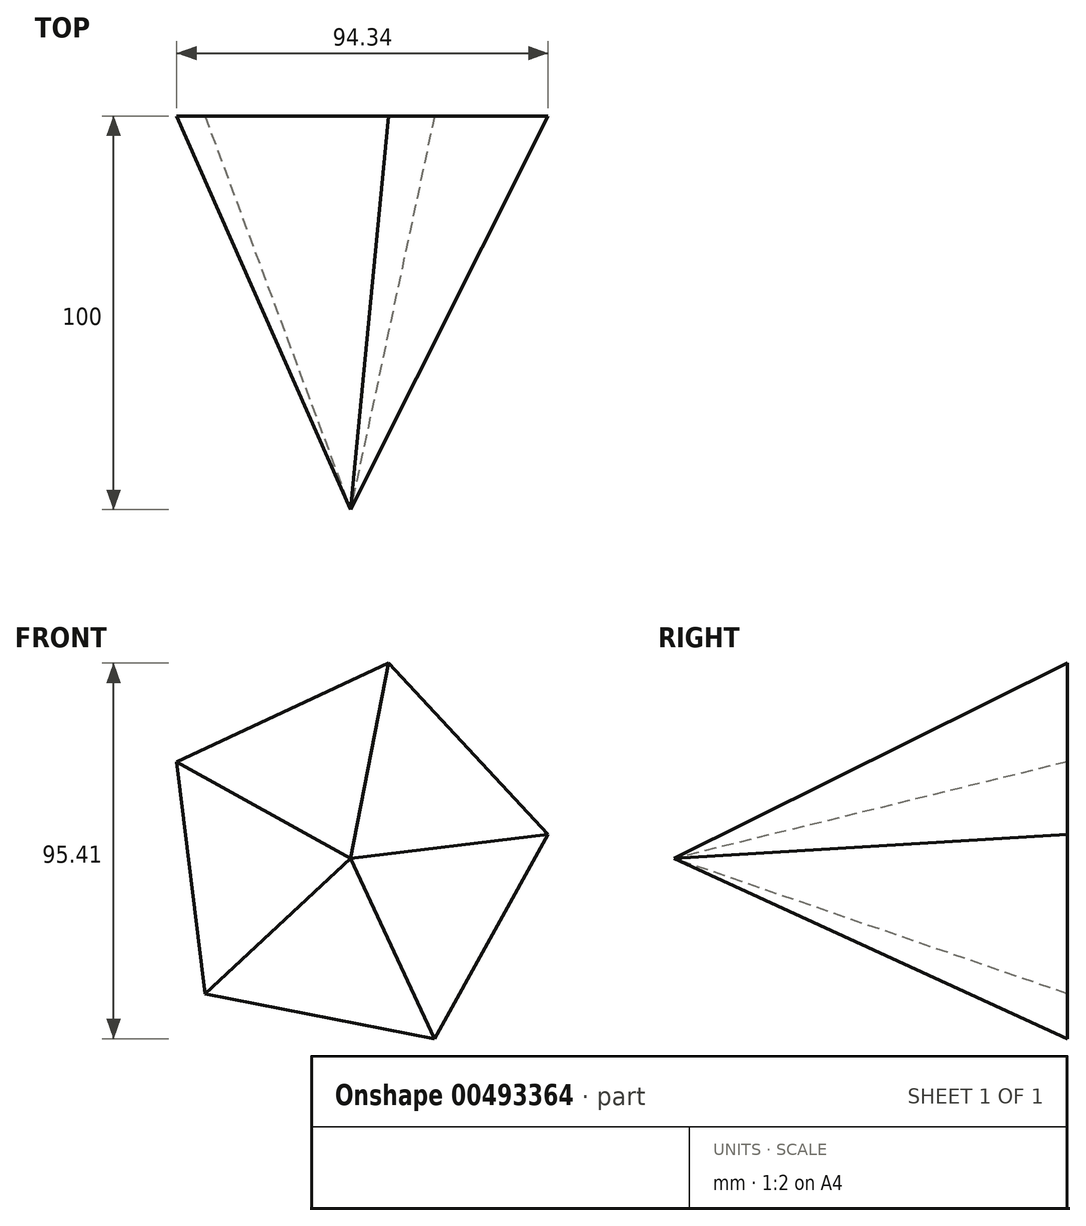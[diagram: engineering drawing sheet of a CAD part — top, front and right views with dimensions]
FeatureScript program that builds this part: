
annotation { "Feature Type Name" : "Feature", "Feature Type Description" : "" }
export const myFeature = defineFeature(function(context is Context, id is Id, definition is map)
    precondition{}
    {
        {
            var Q0;
            Q0=qCreatedBy(makeId("Front.planeOp"),FACE);
            var sketch = newSketch(context, id + "F0", { "sketchPlane" : qUnion([Q0])});
            skCircle(sketch, "E0.cCircle", {"center": v(0, 0) * mm, "radius": 50.53 * mm, "construction": true});
            skLineSegment(sketch, "E0.0", {"start": v(-44.18, 24.53) * mm, "end": v(9.68, 49.6) * mm});
            skLineSegment(sketch, "E0.1", {"start": v(9.68, 49.6) * mm, "end": v(50.16, 6.12) * mm});
            skLineSegment(sketch, "E0.2", {"start": v(50.16, 6.12) * mm, "end": v(21.33, -45.81) * mm});
            skLineSegment(sketch, "E0.3", {"start": v(21.33, -45.81) * mm, "end": v(-36.98, -34.44) * mm});
            skLineSegment(sketch, "E0.4", {"start": v(-36.98, -34.44) * mm, "end": v(-44.18, 24.53) * mm});
            skSolve(sketch);
        }
        {
            var Q0;
            Q0=qCreatedBy(makeId("Front.planeOp"),FACE);
            cPlane(context, id + "F1", {"entities" : qUnion([Q0]), "cplaneType" : CPlaneType.OFFSET, "offset" : 100 * mm, "width" : 150 * mm, "height" : 150 * mm});
        }
        {
            var Q0;
            Q0=qCreatedBy(id+"F1.planeOp",FACE);
            var sketch = newSketch(context, id + "F2", { "sketchPlane" : qUnion([Q0])});
            skPoint(sketch, "E1", {"position": v(0, 0) * mm});
            skSolve(sketch);
        }
        {
            var Q0;
            Q0=makeQuery(id+"F0.imprint","IMPRINT",FACE,{"disambiguationData":[TD([[makeQuery(id+"F0.imprint","IMPRINT",EDGE,{"derivedFrom":sQuery(id+"F0.wireOp",EDGE,"E0.0")}),-1.0]])]});
            var Q1;
            Q1=sQuery(id+"F2.wireOp",VERTEX,"E1");
            loft(context, id + "F3", {"sheetProfilesArray" : [{ "sheetProfileEntities" : qUnion([Q0]) }, { "sheetProfileEntities" : qUnion([Q1]) }]});
        }
    });
